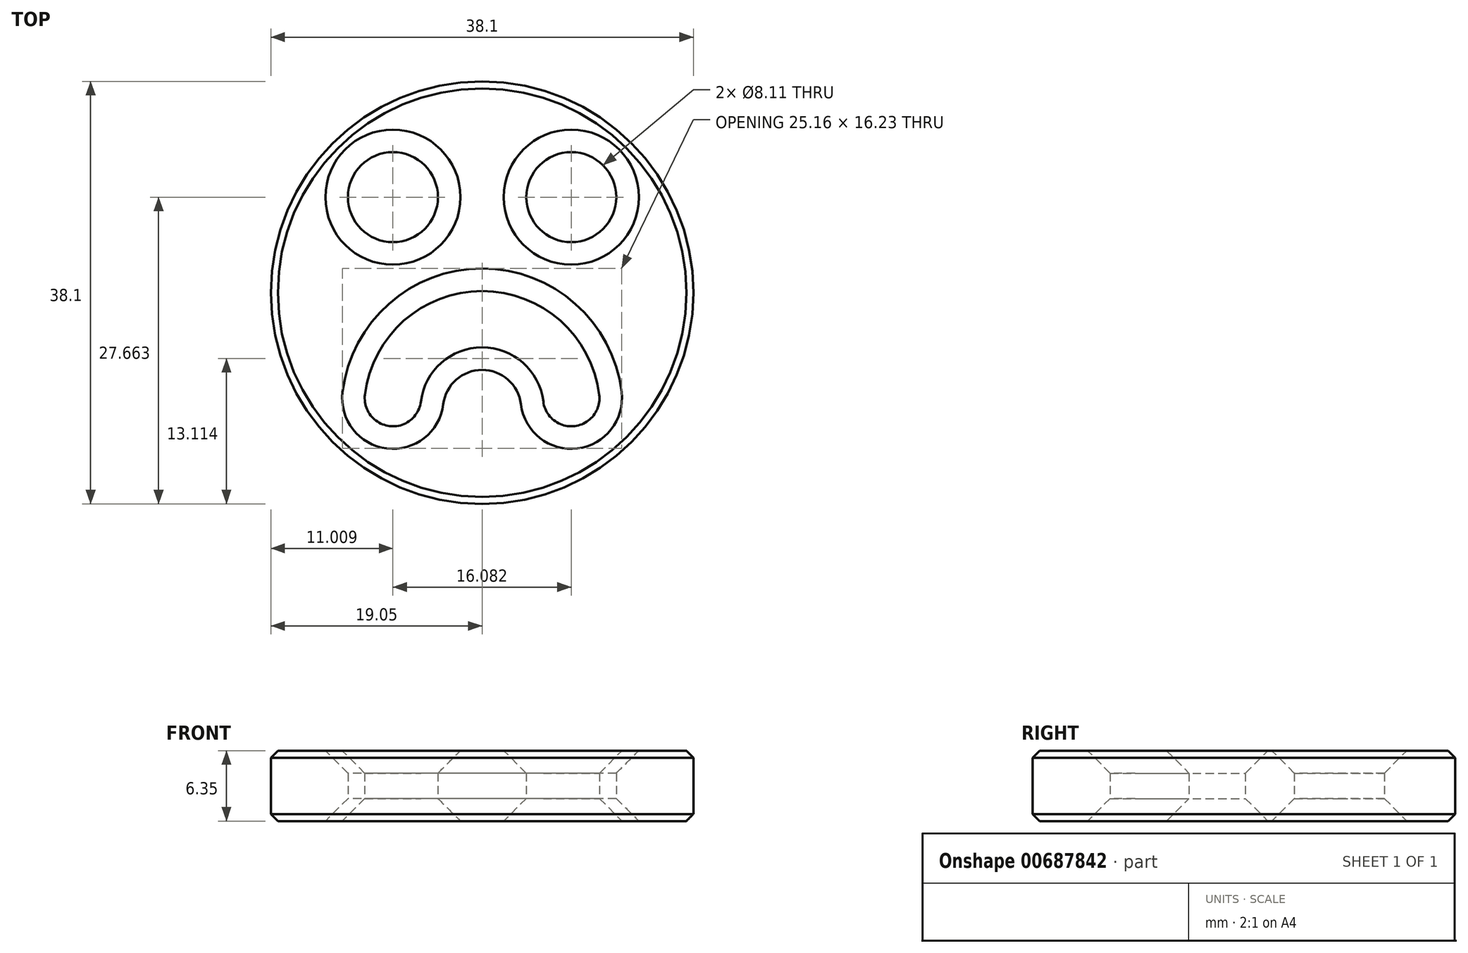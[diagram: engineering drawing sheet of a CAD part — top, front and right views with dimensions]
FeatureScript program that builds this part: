
annotation { "Feature Type Name" : "Feature", "Feature Type Description" : "" }
export const myFeature = defineFeature(function(context is Context, id is Id, definition is map)
    precondition{}
    {
        {
            var Q0;
            Q0=qCreatedBy(makeId("Top.planeOp"),FACE);
            var sketch = newSketch(context, id + "F0", { "sketchPlane" : qUnion([Q0])});
            skCircle(sketch, "E0", {"center": v(0, 0) * mm, "radius": 19.05 * mm});
            skCircle(sketch, "E1", {"center": v(-8.04, 8.61) * mm, "radius": 4.06 * mm});
            skCircle(sketch, "E2.MirrorC", {"center": v(8.04, 8.61) * mm, "radius": 4.06 * mm});
            skArc(sketch, "E3", {"start": v(8.04, -9.51) * mm, "mid": v(0, -2.4) * mm, "end": v(-8.04, -9.51) * mm});
            skArc(sketch, "E4.0.startCap", {"start": v(10.56, -9.2) * mm, "mid": v(8.35, -12.03) * mm, "end": v(5.52, -9.82) * mm});
            skArc(sketch, "E4.0.endCap", {"start": v(-5.52, -9.82) * mm, "mid": v(-8.35, -12.03) * mm, "end": v(-10.56, -9.2) * mm});
            skArc(sketch, "E4.0.left", {"start": v(5.52, -9.82) * mm, "mid": v(0, -4.93) * mm, "end": v(-5.52, -9.82) * mm});
            skArc(sketch, "E4.0.right", {"start": v(10.56, -9.2) * mm, "mid": v(0, 0.15) * mm, "end": v(-10.56, -9.2) * mm});
            skSolve(sketch);
        }
        {
            var Q0;
            Q0=makeQuery(id+"F0.imprint","IMPRINT",FACE,{"disambiguationData":[TD([[makeQuery(id+"F0.imprint","IMPRINT",EDGE,{"derivedFrom":sQuery(id+"F0.wireOp",EDGE,"E0")}),1.0]])]});
            extrude(context, id + "F1", {"entities" : qUnion([Q0]), "depth" : 6.35 * mm, "offsetDistance" : 25.4 * mm});
        }
        {
            var Q0;
            Q0=makeQuery(id+"F1.opExtrude","CAP_EDGE",EDGE,{"disambiguationData":[OSD([sQuery(id+"F0.wireOp",EDGE,"E4.0.right")])],"isStart":false});
            var Q1;
            Q1=makeQuery(id+"F1.opExtrude","CAP_EDGE",EDGE,{"disambiguationData":[OSD([sQuery(id+"F0.wireOp",EDGE,"E4.0.right")])],"isStart":true});
            var Q2;
            Q2=makeQuery(id+"F1.opExtrude","CAP_EDGE",EDGE,{"disambiguationData":[OSD([sQuery(id+"F0.wireOp",EDGE,"E4.0.left")])],"isStart":false});
            var Q3;
            Q3=makeQuery(id+"F1.opExtrude","CAP_EDGE",EDGE,{"disambiguationData":[OSD([sQuery(id+"F0.wireOp",EDGE,"E4.0.startCap")])],"isStart":false});
            var Q4;
            Q4=makeQuery(id+"F1.opExtrude","CAP_EDGE",EDGE,{"disambiguationData":[OSD([sQuery(id+"F0.wireOp",EDGE,"E4.0.endCap")])],"isStart":false});
            var Q5;
            Q5=makeQuery(id+"F1.opExtrude","CAP_EDGE",EDGE,{"disambiguationData":[OSD([sQuery(id+"F0.wireOp",EDGE,"E4.0.startCap")])],"isStart":true});
            var Q6;
            Q6=makeQuery(id+"F1.opExtrude","CAP_EDGE",EDGE,{"disambiguationData":[OSD([sQuery(id+"F0.wireOp",EDGE,"E4.0.left")])],"isStart":true});
            var Q7;
            Q7=makeQuery(id+"F1.opExtrude","CAP_EDGE",EDGE,{"disambiguationData":[OSD([sQuery(id+"F0.wireOp",EDGE,"E4.0.endCap")])],"isStart":true});
            var Q8;
            Q8=makeQuery(id+"F1.opExtrude","CAP_EDGE",EDGE,{"disambiguationData":[OSD([sQuery(id+"F0.wireOp",EDGE,"E2.MirrorC")])],"isStart":false});
            var Q9;
            Q9=makeQuery(id+"F1.opExtrude","CAP_EDGE",EDGE,{"disambiguationData":[OSD([sQuery(id+"F0.wireOp",EDGE,"E2.MirrorC")])],"isStart":true});
            var Q10;
            Q10=makeQuery(id+"F1.opExtrude","CAP_EDGE",EDGE,{"disambiguationData":[OSD([sQuery(id+"F0.wireOp",EDGE,"E1")])],"isStart":true});
            var Q11;
            Q11=makeQuery(id+"F1.opExtrude","CAP_EDGE",EDGE,{"disambiguationData":[OSD([sQuery(id+"F0.wireOp",EDGE,"E1")])],"isStart":false});
            chamfer(context, id + "F2", {"entities" : qUnion([Q0, Q1, Q2, Q3, Q4, Q5, Q6, Q7, Q8, Q9, Q10, Q11]), "width" : 2.03 * mm, "tangentPropagation" : true});
        }
        {
            var Q0;
            Q0=makeQuery(id+"F1.opExtrude","CAP_EDGE",EDGE,{"disambiguationData":[OSD([sQuery(id+"F0.wireOp",EDGE,"E0")])],"isStart":false});
            var Q1;
            Q1=makeQuery(id+"F1.opExtrude","CAP_EDGE",EDGE,{"disambiguationData":[OSD([sQuery(id+"F0.wireOp",EDGE,"E0")])],"isStart":true});
            chamfer(context, id + "F3", {"entities" : qUnion([Q0, Q1]), "width" : 0.64 * mm, "tangentPropagation" : true});
        }
    });
